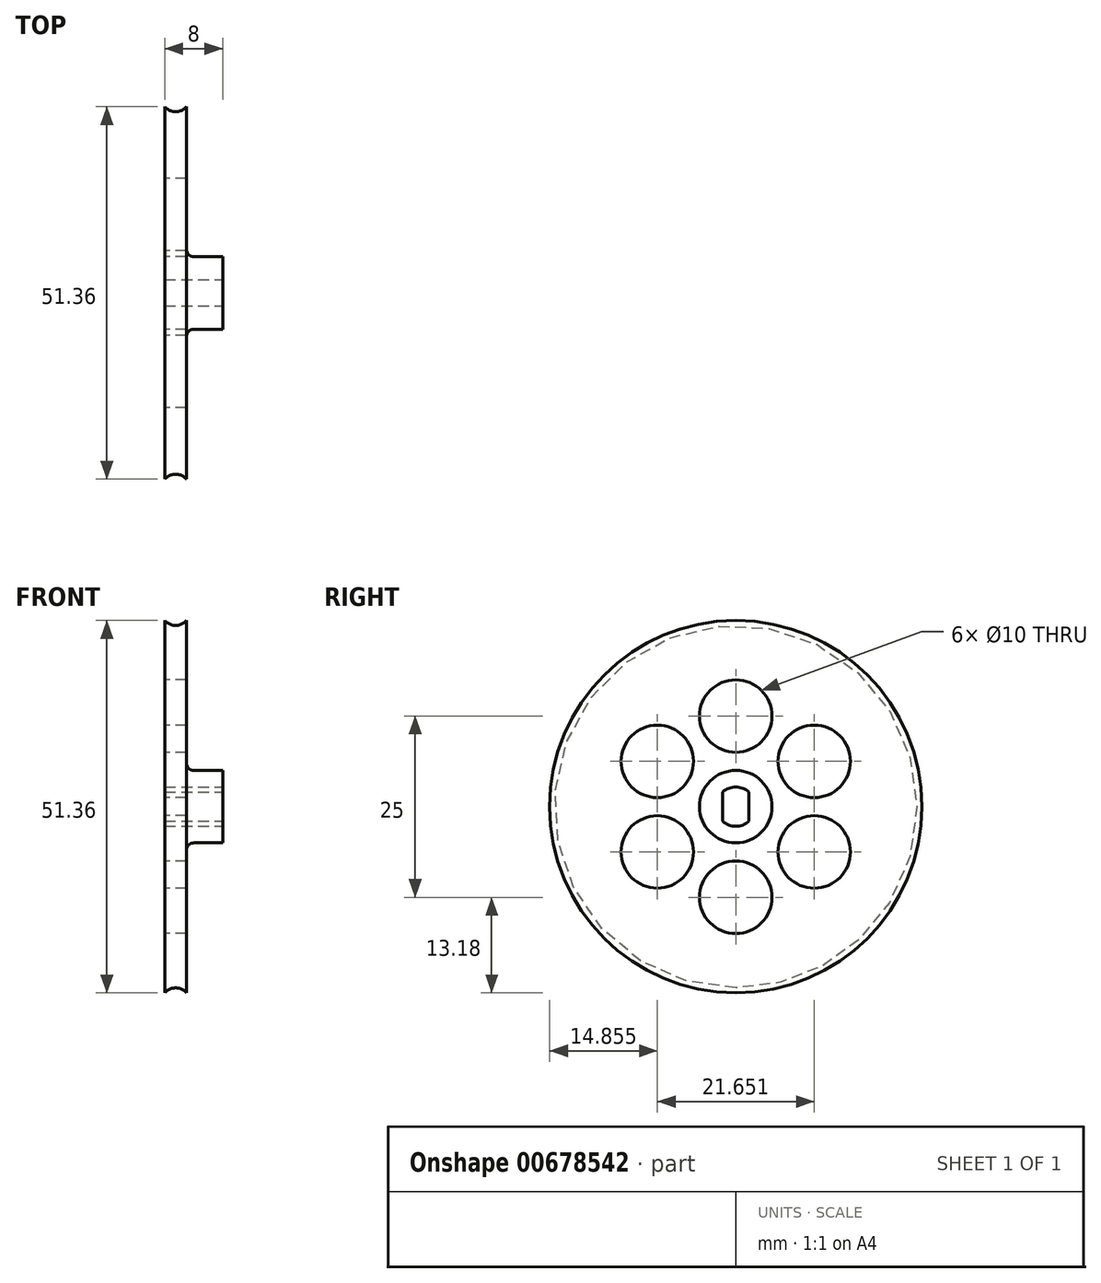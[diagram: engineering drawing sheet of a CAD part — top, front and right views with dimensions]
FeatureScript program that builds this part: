
annotation { "Feature Type Name" : "Feature", "Feature Type Description" : "" }
export const myFeature = defineFeature(function(context is Context, id is Id, definition is map)
    precondition{}
    {
        {
            var Q0;
            Q0=qCreatedBy(makeId("Front.planeOp"),FACE);
            var sketch = newSketch(context, id + "F0", { "sketchPlane" : qUnion([Q0])});
            skLineSegment(sketch, "E0", {"start": v(0, 0) * mm, "end": v(0, 25.68) * mm});
            skLineSegment(sketch, "E1", {"start": v(3, 25.68) * mm, "end": v(3, 6) * mm});
            skLineSegment(sketch, "E2", {"start": v(3, 0) * mm, "end": v(0, 0) * mm});
            skLineSegment(sketch, "E3", {"start": v(1.5, 25.68) * mm, "end": v(1.5, 0) * mm, "construction": true});
            skArc(sketch, "E4", {"start": v(0, 25.68) * mm, "mid": v(1.5, 25) * mm, "end": v(3, 25.68) * mm});
            skLineSegment(sketch, "E5", {"start": v(4, 5) * mm, "end": v(8, 5) * mm});
            skLineSegment(sketch, "E6", {"start": v(8, 5) * mm, "end": v(8, 0) * mm});
            skLineSegment(sketch, "E7", {"start": v(8, 0) * mm, "end": v(3, 0) * mm});
            skPoint(sketch, "E8.newPointB", {"position": v(3, 0) * mm});
            skArc(sketch, "E8.filletArc", {"start": v(3, 6) * mm, "mid": v(3.3, 5.3) * mm, "end": v(4, 5) * mm});
            skSolve(sketch);
        }
        {
            var Q0;
            Q0 = qSketchRegion(id + "F0", true);
            var Q1;
            Q1=sQuery(id+"F0.wireOp",EDGE,"E2");
            revolve(context, id + "F1", {"entities" : qUnion([Q0]), "axis" : qUnion([Q1]), "revolveType" : RevolveType.FULL});
        }
        {
            var Q0;
            Q0=makeQuery(id+"F1.opRevolve","SWEPT_FACE",FACE,{"disambiguationData":[OSD([sQuery(id+"F0.wireOp",EDGE,"E6")])]});
            var sketch = newSketch(context, id + "F2", { "sketchPlane" : qUnion([Q0])});
            skArc(sketch, "E9", {"start": v(-1.8, -2.01) * mm, "mid": v(0, -2.7) * mm, "end": v(1.8, -2.01) * mm});
            skLineSegment(sketch, "E10", {"start": v(-1.8, -2.01) * mm, "end": v(-1.8, 2.01) * mm});
            skLineSegment(sketch, "E11", {"start": v(1.8, -2.01) * mm, "end": v(1.8, 2.01) * mm});
            skArc(sketch, "E12.trimOffspring", {"start": v(1.8, 2.01) * mm, "mid": v(0, 2.7) * mm, "end": v(-1.8, 2.01) * mm});
            skSolve(sketch);
        }
        {
            var Q0;
            Q0=makeQuery(id+"F2.imprint","IMPRINT",FACE,{"disambiguationData":[TD([[makeQuery(id+"F2.imprint","IMPRINT",EDGE,{"derivedFrom":sQuery(id+"F2.wireOp",EDGE,"E9")}),1.0]])]});
            var Q1;
            Q1=makeQuery(id+"F1.opRevolve","SWEPT_FACE",FACE,{"disambiguationData":[OSD([sQuery(id+"F0.wireOp",EDGE,"E0")])]});
            var Q2;
            Q2=sQuery(id+"F0.wireOp",VERTEX,"E0.start");
            extrude(context, id + "F3", {"entities" : qUnion([Q0, Q1]), "operationType" : NewBodyOperationType.REMOVE, "oppositeDirection" : true, "depth" : 8 * mm, "endBoundEntityVertex" : qUnion([Q2]), "offsetDistance" : 25 * mm});
        }
        {
            var Q0;
            Q0=makeQuery(id+"F1.opRevolve","SWEPT_FACE",FACE,{"disambiguationData":[OSD([sQuery(id+"F0.wireOp",EDGE,"E0")])]});
            var sketch = newSketch(context, id + "F4", { "sketchPlane" : qUnion([Q0])});
            skCircle(sketch, "E13", {"center": v(0, 0) * mm, "radius": 12.5 * mm, "construction": true});
            skCircle(sketch, "E14", {"center": v(0, 12.5) * mm, "radius": 5 * mm});
            skCircle(sketch, "E15.1.0", {"center": v(-10.83, 6.25) * mm, "radius": 5 * mm});
            skCircle(sketch, "E15.2.0", {"center": v(-10.83, -6.25) * mm, "radius": 5 * mm});
            skCircle(sketch, "E15.3.0", {"center": v(0, -12.5) * mm, "radius": 5 * mm});
            skCircle(sketch, "E15.4.0", {"center": v(10.83, -6.25) * mm, "radius": 5 * mm});
            skCircle(sketch, "E15.5.0", {"center": v(10.83, 6.25) * mm, "radius": 5 * mm});
            skSolve(sketch);
        }
        {
            var Q0;
            Q0=makeQuery(id+"F4.imprint","IMPRINT",FACE,{"disambiguationData":[TD([[makeQuery(id+"F4.imprint","IMPRINT",EDGE,{"derivedFrom":sQuery(id+"F4.wireOp",EDGE,"E14")}),1.0]])]});
            var Q1;
            Q1=makeQuery(id+"F4.imprint","IMPRINT",FACE,{"disambiguationData":[TD([[makeQuery(id+"F4.imprint","IMPRINT",EDGE,{"derivedFrom":sQuery(id+"F4.wireOp",EDGE,"E15.5.0")}),1.0]])]});
            var Q2;
            Q2=makeQuery(id+"F4.imprint","IMPRINT",FACE,{"disambiguationData":[TD([[makeQuery(id+"F4.imprint","IMPRINT",EDGE,{"derivedFrom":sQuery(id+"F4.wireOp",EDGE,"E15.4.0")}),1.0]])]});
            var Q3;
            Q3=makeQuery(id+"F4.imprint","IMPRINT",FACE,{"disambiguationData":[TD([[makeQuery(id+"F4.imprint","IMPRINT",EDGE,{"derivedFrom":sQuery(id+"F4.wireOp",EDGE,"E15.3.0")}),1.0]])]});
            var Q4;
            Q4=makeQuery(id+"F4.imprint","IMPRINT",FACE,{"disambiguationData":[TD([[makeQuery(id+"F4.imprint","IMPRINT",EDGE,{"derivedFrom":sQuery(id+"F4.wireOp",EDGE,"E15.2.0")}),1.0]])]});
            var Q5;
            Q5=makeQuery(id+"F4.imprint","IMPRINT",FACE,{"disambiguationData":[TD([[makeQuery(id+"F4.imprint","IMPRINT",EDGE,{"derivedFrom":sQuery(id+"F4.wireOp",EDGE,"E15.1.0")}),1.0]])]});
            var Q6;
            Q6=sQuery(id+"F4.wireOp",EDGE,"E14");
            var Q7;
            Q7=sQuery(id+"F4.wireOp",EDGE,"E15.1.0");
            var Q8;
            Q8=sQuery(id+"F4.wireOp",EDGE,"E15.2.0");
            var Q9;
            Q9=sQuery(id+"F4.wireOp",EDGE,"E15.3.0");
            var Q10;
            Q10=sQuery(id+"F4.wireOp",EDGE,"E15.4.0");
            var Q11;
            Q11=sQuery(id+"F4.wireOp",EDGE,"E15.5.0");
            var Q12;
            Q12=makeQuery(id+"F1.opRevolve","SWEPT_FACE",FACE,{"disambiguationData":[OSD([sQuery(id+"F0.wireOp",EDGE,"E1")])]});
            extrude(context, id + "F5", {"entities" : qUnion([Q0, Q1, Q2, Q3, Q4, Q5]), "operationType" : NewBodyOperationType.REMOVE, "surfaceEntities" : qUnion([Q6, Q7, Q8, Q9, Q10, Q11]), "endBound" : BoundingType.UP_TO_SURFACE, "oppositeDirection" : true, "depth" : 25 * mm, "endBoundEntityFace" : qUnion([Q12]), "offsetDistance" : 25 * mm});
        }
    });
